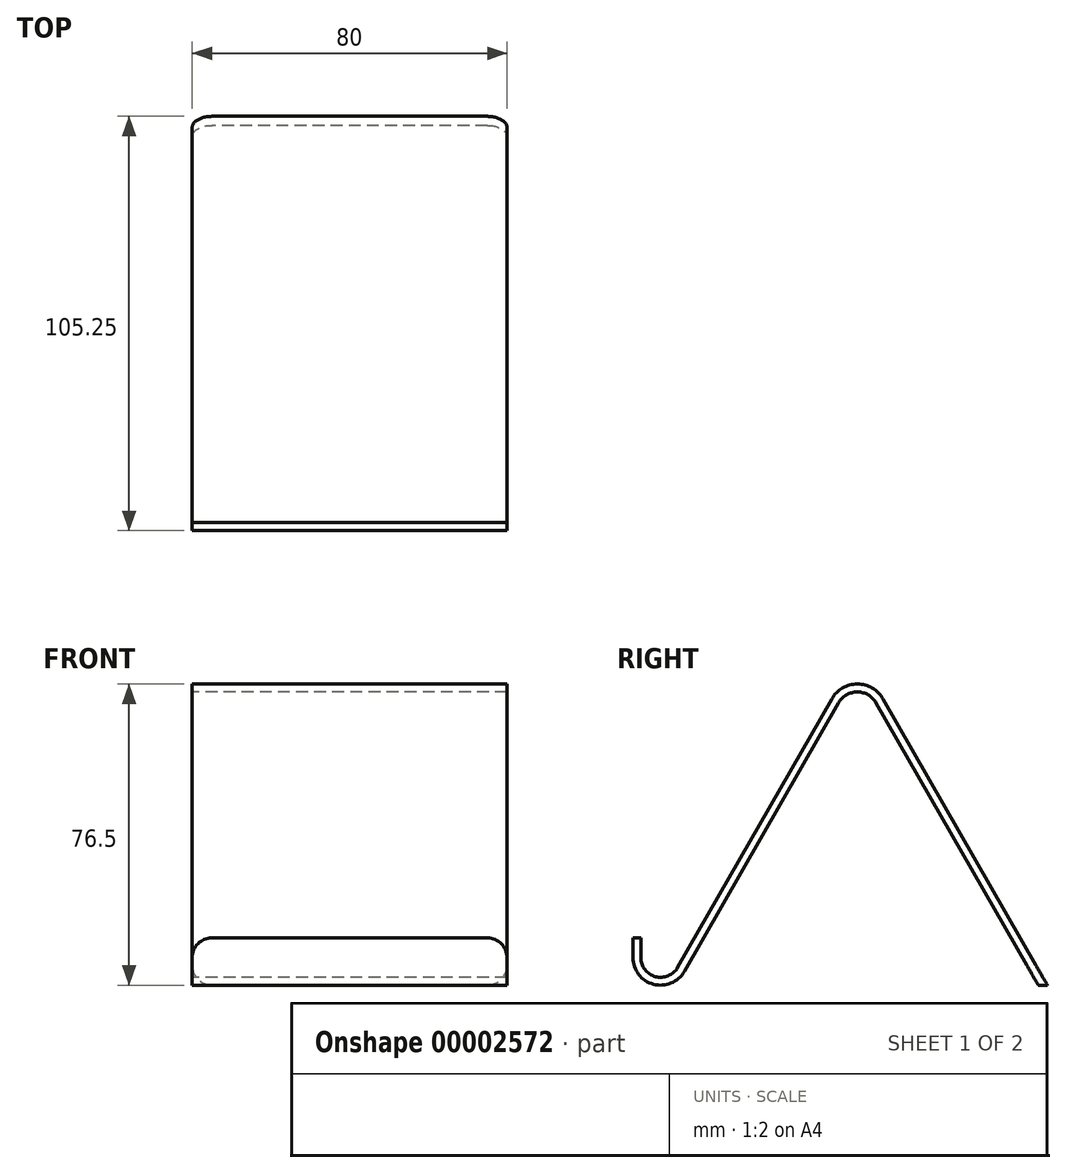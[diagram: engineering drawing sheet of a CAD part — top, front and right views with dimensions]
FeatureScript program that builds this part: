
annotation { "Feature Type Name" : "Feature", "Feature Type Description" : "" }
export const myFeature = defineFeature(function(context is Context, id is Id, definition is map)
    precondition{}
    {
        {
            var Q0;
            Q0=qCreatedBy(makeId("Right.planeOp"),FACE);
            var sketch = newSketch(context, id + "F0", { "sketchPlane" : qUnion([Q0])});
            skArc(sketch, "E0", {"start": v(-7, 0) * mm, "mid": v(-1.8, -6.76) * mm, "end": v(6.07, -3.48) * mm});
            skArc(sketch, "E1", {"start": v(54.77, 64.74) * mm, "mid": v(50, 67.5) * mm, "end": v(45.23, 64.74) * mm});
            skLineSegment(sketch, "E2", {"start": v(6.07, -3.48) * mm, "end": v(45.23, 64.74) * mm});
            skLineSegment(sketch, "E3", {"start": v(50, 62) * mm, "end": v(50, -45.75) * mm, "construction": true});
            skLineSegment(sketch, "E4.0.MirrorCS", {"start": v(95.95, -7) * mm, "end": v(54.77, 64.74) * mm});
            skLineSegment(sketch, "E5", {"start": v(0, -7) * mm, "end": v(136.12, -7) * mm, "construction": true});
            skLineSegment(sketch, "E6", {"start": v(-7, 0) * mm, "end": v(-7, 5) * mm});
            skLineSegment(sketch, "E7.0", {"start": v(-5, 0) * mm, "end": v(-5, 5) * mm});
            skArc(sketch, "E7.1", {"start": v(-5, 0) * mm, "mid": v(-1.29, -4.83) * mm, "end": v(4.34, -2.49) * mm});
            skLineSegment(sketch, "E7.2", {"start": v(4.34, -2.49) * mm, "end": v(43.5, 65.73) * mm});
            skArc(sketch, "E7.3", {"start": v(56.5, 65.73) * mm, "mid": v(50, 69.5) * mm, "end": v(43.5, 65.73) * mm});
            skLineSegment(sketch, "E7.4", {"start": v(98.25, -7) * mm, "end": v(56.5, 65.73) * mm});
            skLineSegment(sketch, "E8", {"start": v(-7, 5) * mm, "end": v(-5, 5) * mm});
            skLineSegment(sketch, "E9", {"start": v(95.95, -7) * mm, "end": v(98.25, -7) * mm});
            skSolve(sketch);
        }
        {
            var Q0;
            Q0=makeQuery(id+"F0.imprint","IMPRINT",FACE,{"disambiguationData":[TD([[makeQuery(id+"F0.imprint","IMPRINT",EDGE,{"derivedFrom":sQuery(id+"F0.wireOp",EDGE,"E0")}),1.0]])]});
            extrude(context, id + "F1", {"entities" : qUnion([Q0]), "depth" : 80 * mm});
        }
        {
            var Q0;
            Q0=makeQuery(id+"F1.opExtrude","CAP_EDGE",EDGE,{"disambiguationData":[OSD([sQuery(id+"F0.wireOp",EDGE,"E8")])],"isStart":false});
            var Q1;
            Q1=makeQuery(id+"F1.opExtrude","CAP_EDGE",EDGE,{"disambiguationData":[OSD([sQuery(id+"F0.wireOp",EDGE,"E8")])],"isStart":true});
            var Q2;
            Q2=makeQuery(id+"F1.opExtrude","CAP_EDGE",EDGE,{"disambiguationData":[OSD([sQuery(id+"F0.wireOp",EDGE,"E9")])],"isStart":true});
            var Q3;
            Q3=makeQuery(id+"F1.opExtrude","CAP_EDGE",EDGE,{"disambiguationData":[OSD([sQuery(id+"F0.wireOp",EDGE,"E9")])],"isStart":false});
            fillet(context, id + "F2", {"entities" : qUnion([Q0, Q1, Q2, Q3]), "radius" : 5 * mm, "tangentPropagation" : true, "allowEdgeOverflow" : false});
        }
    });
